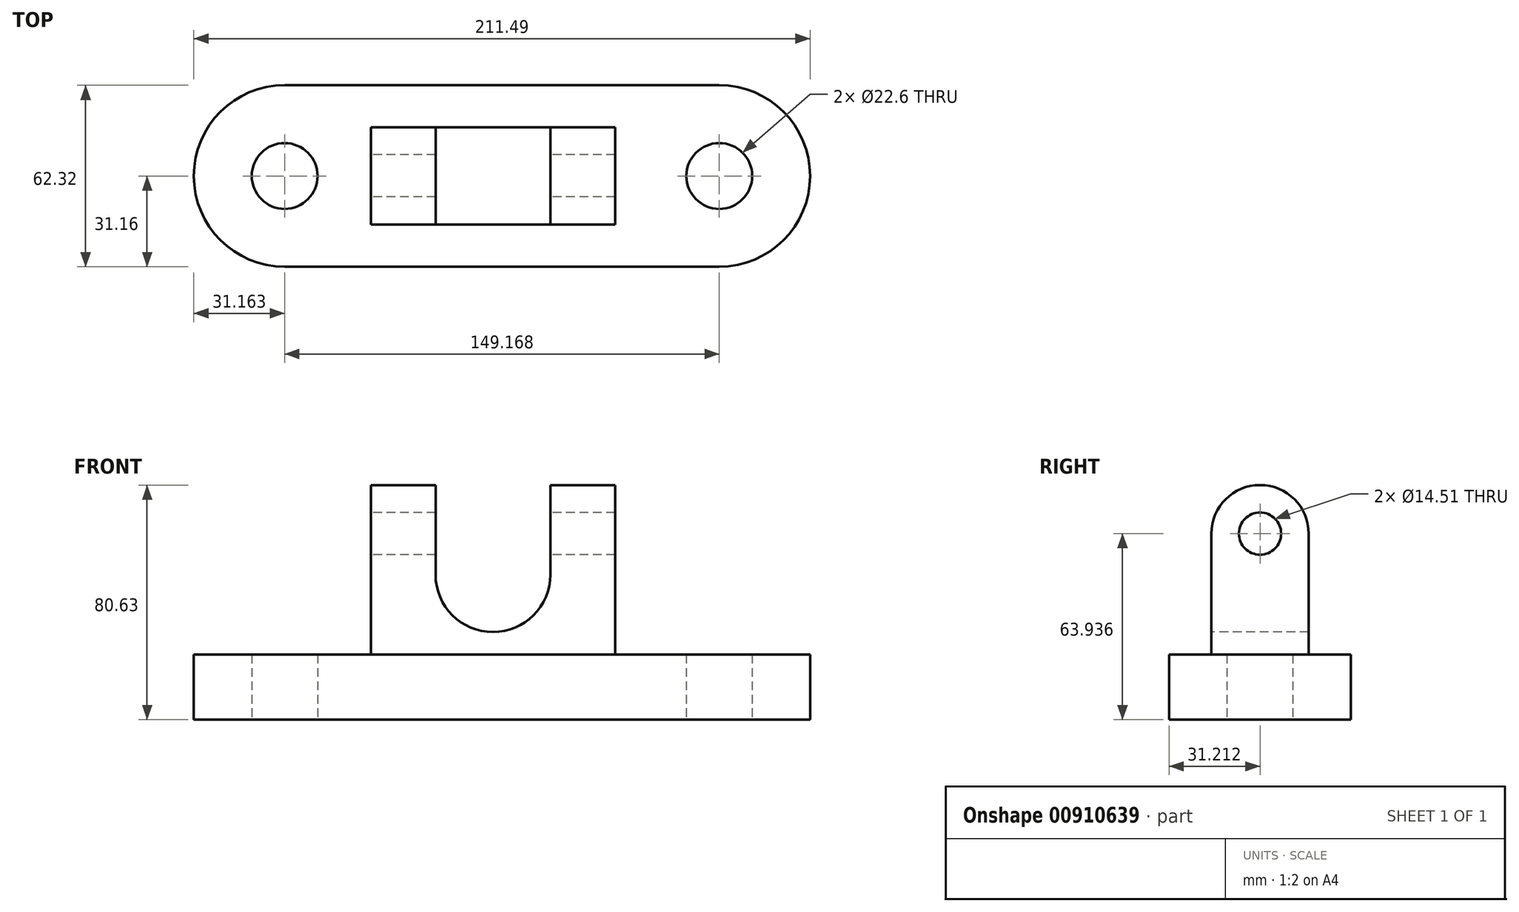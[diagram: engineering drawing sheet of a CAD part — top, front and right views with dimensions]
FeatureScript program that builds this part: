
annotation { "Feature Type Name" : "Feature", "Feature Type Description" : "" }
export const myFeature = defineFeature(function(context is Context, id is Id, definition is map)
    precondition{}
    {
        {
            var Q0;
            Q0=qCreatedBy(makeId("Top.planeOp"),FACE);
            var sketch = newSketch(context, id + "F0", { "sketchPlane" : qUnion([Q0])});
            skLineSegment(sketch, "E0.bottom", {"start": v(77.68, -31.16) * mm, "end": v(-71.49, -31.16) * mm});
            skLineSegment(sketch, "E0.top", {"start": v(77.68, 31.16) * mm, "end": v(-71.49, 31.16) * mm});
            skPoint(sketch, "E0.middle", {"position": v(3.1, 0) * mm});
            skArc(sketch, "E1", {"start": v(-71.49, 31.16) * mm, "mid": v(-102.65, 0) * mm, "end": v(-71.49, -31.16) * mm});
            skArc(sketch, "E2", {"start": v(77.68, -31.16) * mm, "mid": v(108.84, 0) * mm, "end": v(77.68, 31.16) * mm});
            skCircle(sketch, "E3", {"center": v(-71.49, 0) * mm, "radius": 11.3 * mm});
            skCircle(sketch, "E4", {"center": v(77.68, 0) * mm, "radius": 11.3 * mm});
            skSolve(sketch);
        }
        {
            var Q0;
            Q0=qSketchRegion(id+"F0",true);
            extrude(context, id + "F1", {"entities" : qUnion([Q0]), "depth" : 22.35 * mm});
        }
        {
            var Q0;
            Q0=qCreatedBy(makeId("Right.planeOp"),FACE);
            var sketch = newSketch(context, id + "F2", { "sketchPlane" : qUnion([Q0])});
            skLineSegment(sketch, "E5.bottom", {"start": v(-16.64, 0) * mm, "end": v(16.75, 0) * mm});
            skLineSegment(sketch, "E5.left", {"start": v(-16.64, 0) * mm, "end": v(-16.64, 63.94) * mm});
            skLineSegment(sketch, "E5.right", {"start": v(16.75, 0) * mm, "end": v(16.75, 63.94) * mm});
            skArc(sketch, "E6", {"start": v(16.75, 63.94) * mm, "mid": v(0.05, 80.63) * mm, "end": v(-16.64, 63.94) * mm});
            skCircle(sketch, "E7", {"center": v(0.05, 63.94) * mm, "radius": 7.26 * mm});
            skSolve(sketch);
        }
        {
            var Q0;
            Q0=qSketchRegion(id+"F2",true);
            extrude(context, id + "F3", {"entities" : qUnion([Q0]), "operationType" : NewBodyOperationType.ADD, "endBound" : BoundingType.SYMMETRIC, "depth" : 83.82 * mm});
        }
        {
            var Q0;
            Q0=qCreatedBy(makeId("Front.planeOp"),FACE);
            var sketch = newSketch(context, id + "F4", { "sketchPlane" : qUnion([Q0])});
            skLineSegment(sketch, "E8.top", {"start": v(19.7, 113.03) * mm, "end": v(-19.7, 113.03) * mm});
            skLineSegment(sketch, "E8.left", {"start": v(19.7, 49.83) * mm, "end": v(19.7, 113.03) * mm});
            skLineSegment(sketch, "E8.right", {"start": v(-19.7, 49.83) * mm, "end": v(-19.7, 113.03) * mm});
            skPoint(sketch, "E8.middle", {"position": v(0, 81.43) * mm});
            skArc(sketch, "E9", {"start": v(-19.7, 49.83) * mm, "mid": v(0, 30.13) * mm, "end": v(19.7, 49.83) * mm});
            skSolve(sketch);
        }
        {
            var Q0;
            Q0=qSketchRegion(id+"F4",true);
            extrude(context, id + "F5", {"entities" : qUnion([Q0]), "operationType" : NewBodyOperationType.REMOVE, "oppositeDirection" : true, "depth" : 25.4 * mm, "hasSecondDirection" : true, "secondDirectionBound" : SecondDirectionBoundingType.THROUGH_ALL, "secondDirectionOppositeDirection" : false, "secondDirectionDepth" : 25.4 * mm});
        }
    });
